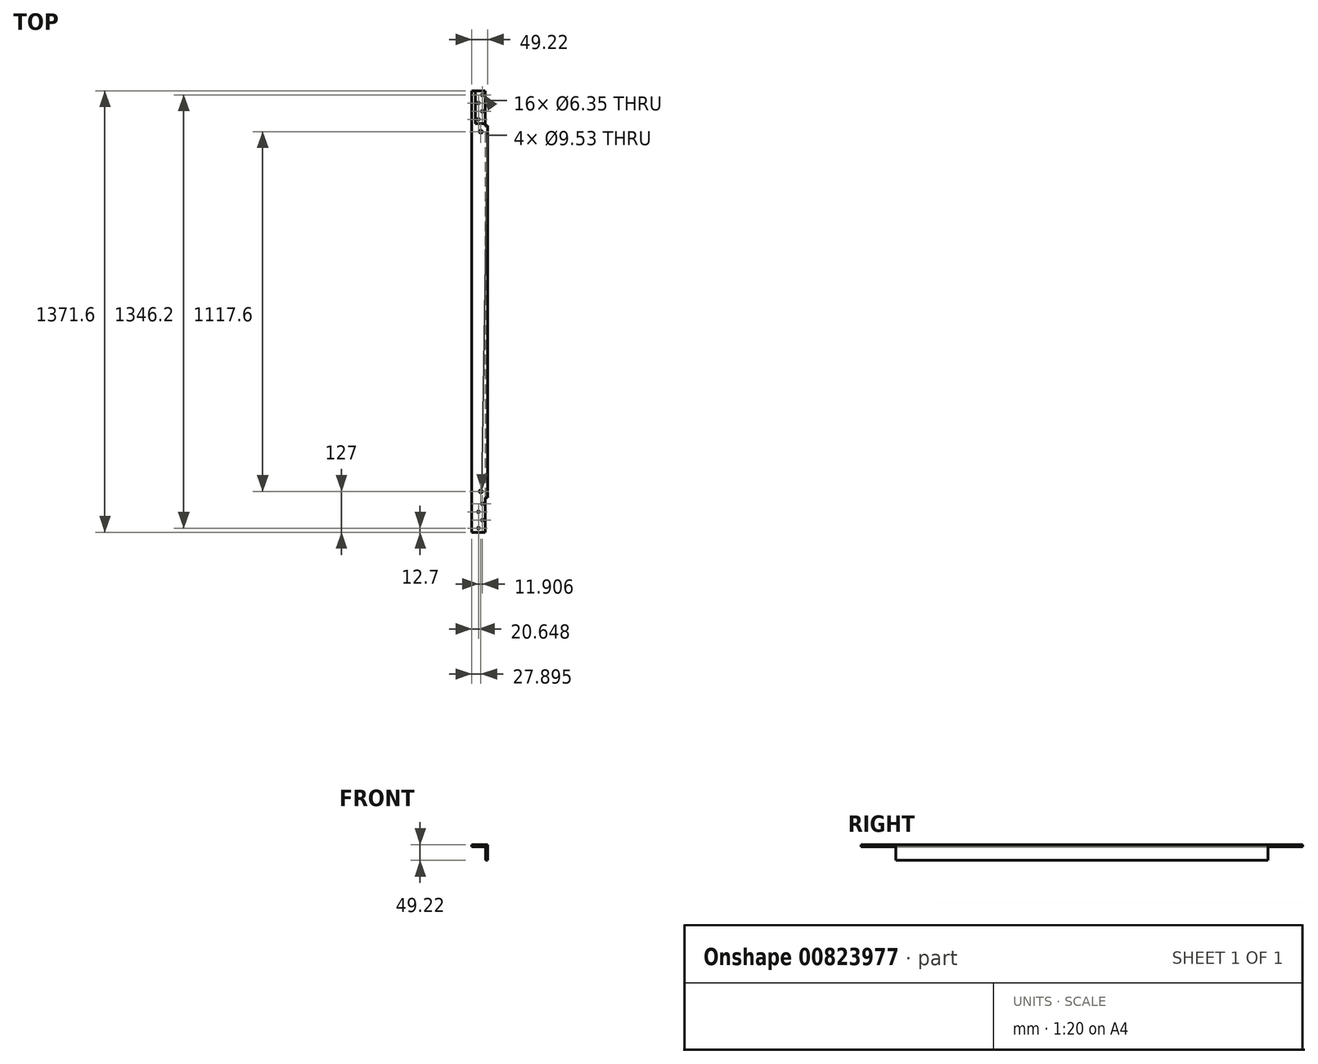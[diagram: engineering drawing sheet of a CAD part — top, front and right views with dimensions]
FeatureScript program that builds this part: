
annotation { "Feature Type Name" : "Feature", "Feature Type Description" : "" }
export const myFeature = defineFeature(function(context is Context, id is Id, definition is map)
    precondition{}
    {
        {
            var Q0;
            Q0=qCreatedBy(makeId("Front.planeOp"),FACE);
            var sketch = newSketch(context, id + "F0", { "sketchPlane" : qUnion([Q0])});
            skLineSegment(sketch, "E0.bottom", {"start": v(24.61, -24.61) * mm, "end": v(18.26, -24.61) * mm});
            skLineSegment(sketch, "E0.top", {"start": v(24.61, 24.61) * mm, "end": v(-24.61, 24.61) * mm});
            skLineSegment(sketch, "E0.left", {"start": v(24.61, -24.61) * mm, "end": v(24.61, 24.61) * mm});
            skLineSegment(sketch, "E0.right", {"start": v(-24.61, 18.26) * mm, "end": v(-24.61, 24.61) * mm});
            skPoint(sketch, "E0.middle", {"position": v(0, 0) * mm});
            skLineSegment(sketch, "E1", {"start": v(-24.61, 18.26) * mm, "end": v(18.26, 18.26) * mm});
            skLineSegment(sketch, "E2", {"start": v(18.26, 18.26) * mm, "end": v(18.26, -24.61) * mm});
            skSolve(sketch);
        }
        {
            var Q0;
            Q0=makeQuery(id+"F0.imprint","IMPRINT",FACE,{"disambiguationData":[TD([[makeQuery(id+"F0.imprint","IMPRINT",EDGE,{"derivedFrom":sQuery(id+"F0.wireOp",EDGE,"E0.bottom")}),-1.0]])]});
            extrude(context, id + "F1", {"entities" : qUnion([Q0]), "endBound" : BoundingType.SYMMETRIC, "depth" : 1371.6 * mm, "offsetDistance" : 25.4 * mm});
        }
        {
            var Q0;
            Q0=makeQuery(id+"F1.opExtrude","SWEPT_FACE",FACE,{"disambiguationData":[OSD([sQuery(id+"F0.wireOp",EDGE,"E0.top")])]});
            var sketch = newSketch(context, id + "F2", { "sketchPlane" : qUnion([Q0])});
            skLineSegment(sketch, "E3.bottom", {"start": v(24.61, -685.8) * mm, "end": v(-13.49, -685.8) * mm});
            skLineSegment(sketch, "E3.top", {"start": v(17.47, -584.2) * mm, "end": v(-13.49, -584.2) * mm});
            skLineSegment(sketch, "E3.right", {"start": v(-13.49, -685.8) * mm, "end": v(-13.49, -584.2) * mm});
            skLineSegment(sketch, "E4.bottom", {"start": v(24.61, -577.85) * mm, "end": v(17.47, -577.85) * mm});
            skLineSegment(sketch, "E4.top", {"start": v(24.61, -685.8) * mm, "end": v(17.47, -685.8) * mm});
            skLineSegment(sketch, "E4.right", {"start": v(17.47, -584.2) * mm, "end": v(17.47, -685.8) * mm});
            skCircle(sketch, "E5", {"center": v(-3.96, -673.1) * mm, "radius": 3.18 * mm});
            skCircle(sketch, "E6", {"center": v(-3.96, -622.3) * mm, "radius": 3.18 * mm});
            skCircle(sketch, "E7", {"center": v(7.94, -647.7) * mm, "radius": 3.18 * mm});
            skCircle(sketch, "E8", {"center": v(7.94, -596.9) * mm, "radius": 3.18 * mm});
            skLineSegment(sketch, "E9", {"start": v(17.47, -577.85) * mm, "end": v(17.47, -584.2) * mm});
            skLineSegment(sketch, "E10", {"start": v(24.61, -577.85) * mm, "end": v(24.61, -685.8) * mm});
            skCircle(sketch, "E11", {"center": v(-3.96, 596.9) * mm, "radius": 3.18 * mm});
            skCircle(sketch, "E12", {"center": v(-3.96, 647.7) * mm, "radius": 3.18 * mm});
            skCircle(sketch, "E13", {"center": v(7.94, 622.3) * mm, "radius": 3.18 * mm});
            skCircle(sketch, "E14", {"center": v(7.94, 673.1) * mm, "radius": 3.18 * mm});
            skLineSegment(sketch, "E15.bottom", {"start": v(24.61, 577.85) * mm, "end": v(17.47, 577.85) * mm});
            skLineSegment(sketch, "E15.top", {"start": v(24.61, 685.8) * mm, "end": v(17.47, 685.8) * mm});
            skLineSegment(sketch, "E15.left", {"start": v(24.61, 577.85) * mm, "end": v(24.61, 685.8) * mm});
            skLineSegment(sketch, "E15.right", {"start": v(17.47, 577.85) * mm, "end": v(17.47, 685.8) * mm});
            skLineSegment(sketch, "E16.bottom", {"start": v(17.47, 584.2) * mm, "end": v(-13.49, 584.2) * mm});
            skLineSegment(sketch, "E16.top", {"start": v(17.47, 685.8) * mm, "end": v(-13.49, 685.8) * mm});
            skLineSegment(sketch, "E16.left", {"start": v(17.47, 584.2) * mm, "end": v(17.47, 685.8) * mm});
            skLineSegment(sketch, "E16.right", {"start": v(-13.49, 584.2) * mm, "end": v(-13.49, 685.8) * mm});
            skSolve(sketch);
        }
        {
            var Q0;
            Q0=makeQuery(id+"F2.imprint","IMPRINT",FACE,{"disambiguationData":[TD([[makeQuery(id+"F2.imprint","IMPRINT",EDGE,{"derivedFrom":sQuery(id+"F2.wireOp",EDGE,"E3.bottom")}),-1.0]])]});
            var Q1;
            Q1=makeQuery(id+"F2.imprint","IMPRINT",FACE,{"disambiguationData":[TD([[makeQuery(id+"F2.imprint","IMPRINT",EDGE,{"derivedFrom":sQuery(id+"F2.wireOp",EDGE,"E11")}),-1.0]])]});
            extrude(context, id + "F3", {"entities" : qUnion([Q0, Q1]), "operationType" : NewBodyOperationType.REMOVE, "oppositeDirection" : true, "depth" : 3.17 * mm, "offsetDistance" : 25.4 * mm});
        }
        {
            var Q0;
            Q0=makeQuery(id+"F2.imprint","IMPRINT",FACE,{"disambiguationData":[TD([[makeQuery(id+"F2.imprint","IMPRINT",EDGE,{"derivedFrom":sQuery(id+"F2.wireOp",EDGE,"E15.bottom")}),-1.0]])]});
            var Q1;
            Q1=makeQuery(id+"F2.imprint","IMPRINT",FACE,{"disambiguationData":[TD([[makeQuery(id+"F2.imprint","IMPRINT",EDGE,{"derivedFrom":sQuery(id+"F2.wireOp",EDGE,"E4.bottom")}),1.0]])]});
            extrude(context, id + "F4", {"entities" : qUnion([Q0, Q1]), "operationType" : NewBodyOperationType.REMOVE, "endBound" : BoundingType.THROUGH_ALL, "oppositeDirection" : true, "depth" : 25.4 * mm, "offsetDistance" : 25.4 * mm});
        }
        {
            var Q0;
            Q0=sQuery(id+"F2.wireOp",VERTEX,"E7.center");
            var Q1;
            Q1=sQuery(id+"F2.wireOp",VERTEX,"E5.center");
            var Q2;
            Q2=sQuery(id+"F2.wireOp",VERTEX,"E6.center");
            var Q3;
            Q3=sQuery(id+"F2.wireOp",VERTEX,"E8.center");
            var Q4;
            Q4=sQuery(id+"F2.wireOp",VERTEX,"E12.center");
            var Q5;
            Q5=sQuery(id+"F2.wireOp",VERTEX,"E14.center");
            var Q6;
            Q6=sQuery(id+"F2.wireOp",VERTEX,"E13.center");
            var Q7;
            Q7=sQuery(id+"F2.wireOp",VERTEX,"E11.center");
            var Q8;
            Q8=makeQuery(id+"F1.opExtrude","SWEPT_BODY",BODY,{"disambiguationData":[OSD([sQuery(id+"F0.wireOp",EDGE,"E0.bottom"),sQuery(id+"F0.wireOp",EDGE,"E0.top"),sQuery(id+"F0.wireOp",EDGE,"E0.left"),sQuery(id+"F0.wireOp",EDGE,"E0.right"),sQuery(id+"F0.wireOp",EDGE,"E1"),sQuery(id+"F0.wireOp",EDGE,"E2")])]});
            hole(context, id + "F5", {"style" : HoleStyle.SIMPLE, "endStyle" : HoleEndStyle.THROUGH, "holeDiameter" : 6.35 * mm, "majorDiameter" : 6.35 * mm, "isTappedThrough" : true, "tappedDepth" : 12.7 * mm, "tapClearance" : 3, "locations" : qUnion([Q0, Q1, Q2, Q3, Q4, Q5, Q6, Q7]), "scope" : qUnion([Q8])});
        }
        {
            var Q0;
            {var subQ1=sQuery(id+"F0.wireOp",EDGE,"E0.left");var subQ4=sQuery(id+"F0.wireOp",EDGE,"E0.top");Q0=makeQuery(id+"F3.boolean.opBoolean","SPLIT",FACE,{"disambiguationData":[TD([makeQuery(id+"F1.opExtrude","SWEPT_FACE",FACE,{"disambiguationData":[OSD([subQ1])]})])],"derivedFrom":makeQuery(id+"F1.opExtrude","SWEPT_FACE",FACE,{"disambiguationData":[OSD([subQ4])]})});}
            var sketch = newSketch(context, id + "F6", { "sketchPlane" : qUnion([Q0])});
            skCircle(sketch, "E17", {"center": v(3.28, 558.8) * mm, "radius": 4.76 * mm});
            skCircle(sketch, "E18.MirrorC", {"center": v(3.28, -558.8) * mm, "radius": 4.76 * mm});
            skSolve(sketch);
        }
        {
            var Q0;
            Q0=sQuery(id+"F6.wireOp",VERTEX,"E18.MirrorC.center");
            var Q1;
            Q1=sQuery(id+"F6.wireOp",VERTEX,"E17.center");
            var Q2;
            Q2=makeQuery(id+"F1.opExtrude","SWEPT_BODY",BODY,{"disambiguationData":[OSD([sQuery(id+"F0.wireOp",EDGE,"E0.bottom"),sQuery(id+"F0.wireOp",EDGE,"E0.top"),sQuery(id+"F0.wireOp",EDGE,"E0.left"),sQuery(id+"F0.wireOp",EDGE,"E0.right"),sQuery(id+"F0.wireOp",EDGE,"E1"),sQuery(id+"F0.wireOp",EDGE,"E2")])]});
            hole(context, id + "F7", {"style" : HoleStyle.SIMPLE, "endStyle" : HoleEndStyle.THROUGH, "holeDiameter" : 9.52 * mm, "majorDiameter" : 6.35 * mm, "isTappedThrough" : true, "tappedDepth" : 12.7 * mm, "tapClearance" : 3, "locations" : qUnion([Q0, Q1]), "scope" : qUnion([Q2])});
        }
    });
